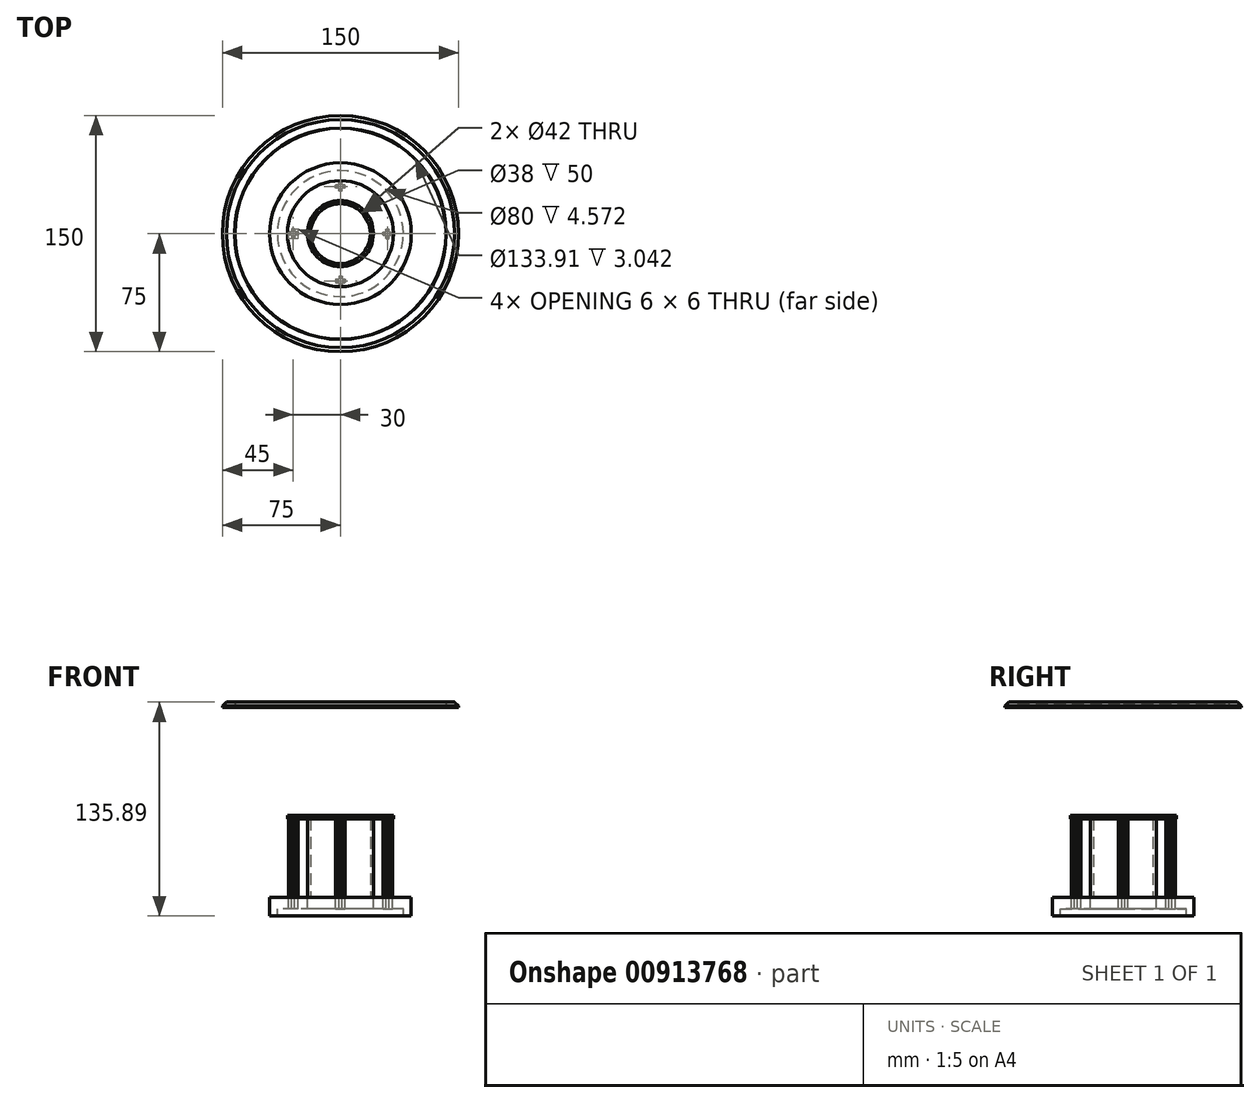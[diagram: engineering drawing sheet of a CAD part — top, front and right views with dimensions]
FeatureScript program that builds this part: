
annotation { "Feature Type Name" : "Feature", "Feature Type Description" : "" }
export const myFeature = defineFeature(function(context is Context, id is Id, definition is map)
    precondition{}
    {
        {
            var Q0;
            Q0=qCreatedBy(makeId("Top.planeOp"),FACE);
            var sketch = newSketch(context, id + "F0", { "sketchPlane" : qUnion([Q0])});
            skLineSegment(sketch, "E0.bottom", {"start": v(3, 29) * mm, "end": v(-3, 29) * mm});
            skLineSegment(sketch, "E0.top", {"start": v(3, 31) * mm, "end": v(-3, 31) * mm});
            skLineSegment(sketch, "E0.left", {"start": v(3, 29) * mm, "end": v(3, 31) * mm});
            skLineSegment(sketch, "E0.right", {"start": v(-3, 29) * mm, "end": v(-3, 31) * mm});
            skPoint(sketch, "E0.middle", {"position": v(0, 30) * mm});
            skLineSegment(sketch, "E1.bottom", {"start": v(1, 27) * mm, "end": v(-1, 27) * mm});
            skLineSegment(sketch, "E1.top", {"start": v(1, 33) * mm, "end": v(-1, 33) * mm});
            skLineSegment(sketch, "E1.left", {"start": v(1, 27) * mm, "end": v(1, 33) * mm});
            skLineSegment(sketch, "E1.right", {"start": v(-1, 27) * mm, "end": v(-1, 33) * mm});
            skLineSegment(sketch, "E2.1.0", {"start": v(-27, 1) * mm, "end": v(-27, -1) * mm});
            skLineSegment(sketch, "E2.1.1", {"start": v(-27, -1) * mm, "end": v(-33, -1) * mm});
            skLineSegment(sketch, "E2.1.2", {"start": v(-29, 3) * mm, "end": v(-29, -3) * mm});
            skLineSegment(sketch, "E2.1.3", {"start": v(-33, 1) * mm, "end": v(-33, -1) * mm});
            skLineSegment(sketch, "E2.1.4", {"start": v(-29, -3) * mm, "end": v(-31, -3) * mm});
            skLineSegment(sketch, "E2.1.5", {"start": v(-29, 3) * mm, "end": v(-31, 3) * mm});
            skLineSegment(sketch, "E2.1.6", {"start": v(-27, 1) * mm, "end": v(-33, 1) * mm});
            skLineSegment(sketch, "E2.1.7", {"start": v(-31, 3) * mm, "end": v(-31, -3) * mm});
            skPoint(sketch, "E2.1.8", {"position": v(-30, 0) * mm});
            skPoint(sketch, "E2.1.9", {"position": v(-30, 0) * mm});
            skLineSegment(sketch, "E2.2.0", {"start": v(-1, -27) * mm, "end": v(1, -27) * mm});
            skLineSegment(sketch, "E2.2.1", {"start": v(1, -27) * mm, "end": v(1, -33) * mm});
            skLineSegment(sketch, "E2.2.2", {"start": v(-3, -29) * mm, "end": v(3, -29) * mm});
            skLineSegment(sketch, "E2.2.3", {"start": v(-1, -33) * mm, "end": v(1, -33) * mm});
            skLineSegment(sketch, "E2.2.4", {"start": v(3, -29) * mm, "end": v(3, -31) * mm});
            skLineSegment(sketch, "E2.2.5", {"start": v(-3, -29) * mm, "end": v(-3, -31) * mm});
            skLineSegment(sketch, "E2.2.6", {"start": v(-1, -27) * mm, "end": v(-1, -33) * mm});
            skLineSegment(sketch, "E2.2.7", {"start": v(-3, -31) * mm, "end": v(3, -31) * mm});
            skPoint(sketch, "E2.2.8", {"position": v(0, -30) * mm});
            skPoint(sketch, "E2.2.9", {"position": v(0, -30) * mm});
            skLineSegment(sketch, "E2.3.0", {"start": v(27, -1) * mm, "end": v(27, 1) * mm});
            skLineSegment(sketch, "E2.3.1", {"start": v(27, 1) * mm, "end": v(33, 1) * mm});
            skLineSegment(sketch, "E2.3.2", {"start": v(29, -3) * mm, "end": v(29, 3) * mm});
            skLineSegment(sketch, "E2.3.3", {"start": v(33, -1) * mm, "end": v(33, 1) * mm});
            skLineSegment(sketch, "E2.3.4", {"start": v(29, 3) * mm, "end": v(31, 3) * mm});
            skLineSegment(sketch, "E2.3.5", {"start": v(29, -3) * mm, "end": v(31, -3) * mm});
            skLineSegment(sketch, "E2.3.6", {"start": v(27, -1) * mm, "end": v(33, -1) * mm});
            skLineSegment(sketch, "E2.3.7", {"start": v(31, -3) * mm, "end": v(31, 3) * mm});
            skPoint(sketch, "E2.3.8", {"position": v(30, 0) * mm});
            skPoint(sketch, "E2.3.9", {"position": v(30, 0) * mm});
            skPoint(sketch, "E2.center", {"position": v(0, 0) * mm});
            skCircle(sketch, "E3", {"center": v(0, 0) * mm, "radius": 21 * mm});
            skCircle(sketch, "E4", {"center": v(0, 0) * mm, "radius": 19 * mm});
            skCircle(sketch, "E5", {"center": v(0, 0) * mm, "radius": 45 * mm});
            skCircle(sketch, "E6", {"center": v(0, 0) * mm, "radius": 40 * mm});
            skCircle(sketch, "E7", {"center": v(0, 0) * mm, "radius": 10.99 * mm});
            skSolve(sketch);
        }
        {
            var Q0;
            {var subQ0=sQuery(id+"F0.wireOp",EDGE,"E0.right");Q0=makeQuery(id+"F0.imprint","IMPRINT",FACE,{"disambiguationData":[TD([[makeQuery(id+"F0.imprint","IMPRINT",EDGE,{"derivedFrom":subQ0}),-1.0]])]});}
            var Q1;
            {var subQ5=sQuery(id+"F0.wireOp",EDGE,"E1.top");Q1=makeQuery(id+"F0.imprint","IMPRINT",FACE,{"disambiguationData":[TD([[makeQuery(id+"F0.imprint","IMPRINT",EDGE,{"derivedFrom":subQ5}),1.0]])]});}
            var Q2;
            {var subQ0=sQuery(id+"F0.wireOp",EDGE,"E0.left");Q2=makeQuery(id+"F0.imprint","IMPRINT",FACE,{"disambiguationData":[TD([[makeQuery(id+"F0.imprint","IMPRINT",EDGE,{"derivedFrom":subQ0}),1.0]])]});}
            var Q3;
            {var subQ5=sQuery(id+"F0.wireOp",EDGE,"E1.bottom");Q3=makeQuery(id+"F0.imprint","IMPRINT",FACE,{"disambiguationData":[TD([[makeQuery(id+"F0.imprint","IMPRINT",EDGE,{"derivedFrom":subQ5}),-1.0]])]});}
            var Q4;
            {var subQ0=sQuery(id+"F0.wireOp",EDGE,"E1.left");var subQ1=sQuery(id+"F0.wireOp",EDGE,"E0.bottom");var subQ2=makeQuery(id+"F0.imprint","INTERSECT",VERTEX,{"derivedFrom":[subQ1,subQ0]});Q4=makeQuery(id+"F0.imprint","IMPRINT",FACE,{"disambiguationData":[TD([[makeQuery(id+"F0.imprint","IMPRINT",EDGE,{"disambiguationData":[TD([[subQ2,-1.0]])],"derivedFrom":subQ1}),-1.0]])]});}
            var Q5;
            {var subQ0=sQuery(id+"F0.wireOp",EDGE,"E2.3.3");Q5=makeQuery(id+"F0.imprint","IMPRINT",FACE,{"disambiguationData":[TD([[makeQuery(id+"F0.imprint","IMPRINT",EDGE,{"derivedFrom":subQ0}),1.0]])]});}
            var Q6;
            {var subQ0=sQuery(id+"F0.wireOp",EDGE,"E2.3.0");Q6=makeQuery(id+"F0.imprint","IMPRINT",FACE,{"disambiguationData":[TD([[makeQuery(id+"F0.imprint","IMPRINT",EDGE,{"derivedFrom":subQ0}),-1.0]])]});}
            var Q7;
            {var subQ0=sQuery(id+"F0.wireOp",EDGE,"E2.3.5");Q7=makeQuery(id+"F0.imprint","IMPRINT",FACE,{"disambiguationData":[TD([[makeQuery(id+"F0.imprint","IMPRINT",EDGE,{"derivedFrom":subQ0}),1.0]])]});}
            var Q8;
            {var subQ5=sQuery(id+"F0.wireOp",EDGE,"E2.3.4");Q8=makeQuery(id+"F0.imprint","IMPRINT",FACE,{"disambiguationData":[TD([[makeQuery(id+"F0.imprint","IMPRINT",EDGE,{"derivedFrom":subQ5}),-1.0]])]});}
            var Q9;
            {var subQ0=sQuery(id+"F0.wireOp",EDGE,"E2.3.2");var subQ1=sQuery(id+"F0.wireOp",EDGE,"E2.3.1");var subQ2=makeQuery(id+"F0.imprint","INTERSECT",VERTEX,{"derivedFrom":[subQ1,subQ0]});Q9=makeQuery(id+"F0.imprint","IMPRINT",FACE,{"disambiguationData":[TD([[makeQuery(id+"F0.imprint","IMPRINT",EDGE,{"disambiguationData":[TD([[subQ2,-1.0]])],"derivedFrom":subQ1}),-1.0]])]});}
            var Q10;
            {var subQ0=sQuery(id+"F0.wireOp",EDGE,"E2.2.0");Q10=makeQuery(id+"F0.imprint","IMPRINT",FACE,{"disambiguationData":[TD([[makeQuery(id+"F0.imprint","IMPRINT",EDGE,{"derivedFrom":subQ0}),-1.0]])]});}
            var Q11;
            {var subQ5=sQuery(id+"F0.wireOp",EDGE,"E2.2.4");Q11=makeQuery(id+"F0.imprint","IMPRINT",FACE,{"disambiguationData":[TD([[makeQuery(id+"F0.imprint","IMPRINT",EDGE,{"derivedFrom":subQ5}),-1.0]])]});}
            var Q12;
            {var subQ0=sQuery(id+"F0.wireOp",EDGE,"E2.2.5");Q12=makeQuery(id+"F0.imprint","IMPRINT",FACE,{"disambiguationData":[TD([[makeQuery(id+"F0.imprint","IMPRINT",EDGE,{"derivedFrom":subQ0}),1.0]])]});}
            var Q13;
            {var subQ0=sQuery(id+"F0.wireOp",EDGE,"E2.2.3");Q13=makeQuery(id+"F0.imprint","IMPRINT",FACE,{"disambiguationData":[TD([[makeQuery(id+"F0.imprint","IMPRINT",EDGE,{"derivedFrom":subQ0}),1.0]])]});}
            var Q14;
            {var subQ0=sQuery(id+"F0.wireOp",EDGE,"E2.2.2");var subQ1=sQuery(id+"F0.wireOp",EDGE,"E2.2.1");var subQ2=makeQuery(id+"F0.imprint","INTERSECT",VERTEX,{"derivedFrom":[subQ1,subQ0]});Q14=makeQuery(id+"F0.imprint","IMPRINT",FACE,{"disambiguationData":[TD([[makeQuery(id+"F0.imprint","IMPRINT",EDGE,{"disambiguationData":[TD([[subQ2,-1.0]])],"derivedFrom":subQ1}),-1.0]])]});}
            var Q15;
            {var subQ0=sQuery(id+"F0.wireOp",EDGE,"E2.1.5");Q15=makeQuery(id+"F0.imprint","IMPRINT",FACE,{"disambiguationData":[TD([[makeQuery(id+"F0.imprint","IMPRINT",EDGE,{"derivedFrom":subQ0}),1.0]])]});}
            var Q16;
            {var subQ0=sQuery(id+"F0.wireOp",EDGE,"E2.1.3");Q16=makeQuery(id+"F0.imprint","IMPRINT",FACE,{"disambiguationData":[TD([[makeQuery(id+"F0.imprint","IMPRINT",EDGE,{"derivedFrom":subQ0}),1.0]])]});}
            var Q17;
            {var subQ0=sQuery(id+"F0.wireOp",EDGE,"E2.1.0");Q17=makeQuery(id+"F0.imprint","IMPRINT",FACE,{"disambiguationData":[TD([[makeQuery(id+"F0.imprint","IMPRINT",EDGE,{"derivedFrom":subQ0}),-1.0]])]});}
            var Q18;
            {var subQ5=sQuery(id+"F0.wireOp",EDGE,"E2.1.4");Q18=makeQuery(id+"F0.imprint","IMPRINT",FACE,{"disambiguationData":[TD([[makeQuery(id+"F0.imprint","IMPRINT",EDGE,{"derivedFrom":subQ5}),-1.0]])]});}
            var Q19;
            {var subQ0=sQuery(id+"F0.wireOp",EDGE,"E2.1.2");var subQ1=sQuery(id+"F0.wireOp",EDGE,"E2.1.1");var subQ2=makeQuery(id+"F0.imprint","INTERSECT",VERTEX,{"derivedFrom":[subQ1,subQ0]});Q19=makeQuery(id+"F0.imprint","IMPRINT",FACE,{"disambiguationData":[TD([[makeQuery(id+"F0.imprint","IMPRINT",EDGE,{"disambiguationData":[TD([[subQ2,-1.0]])],"derivedFrom":subQ1}),-1.0]])]});}
            extrude(context, id + "F1", {"entities" : qUnion([Q0, Q1, Q2, Q3, Q4, Q5, Q6, Q7, Q8, Q9, Q10, Q11, Q12, Q13, Q14, Q15, Q16, Q17, Q18, Q19]), "depth" : 50 * mm, "offsetDistance" : 25.4 * mm});
        }
        {
            var Q0;
            Q0=makeQuery(id+"F0.imprint","IMPRINT",FACE,{"disambiguationData":[TD([[makeQuery(id+"F0.imprint","IMPRINT",EDGE,{"derivedFrom":sQuery(id+"F0.wireOp",EDGE,"E3")}),1.0]])]});
            extrude(context, id + "F2", {"entities" : qUnion([Q0]), "depth" : 50 * mm, "offsetDistance" : 25.4 * mm});
        }
        {
            var Q0;
            Q0=makeQuery(id+"F2.opExtrude","CAP_FACE",FACE,{"disambiguationData":[OSD([sQuery(id+"F0.wireOp",EDGE,"E3"),sQuery(id+"F0.wireOp",EDGE,"E4")])],"isStart":false});
            var sketch = newSketch(context, id + "F3", { "sketchPlane" : qUnion([Q0])});
            skCircle(sketch, "E8", {"center": v(0, 0) * mm, "radius": 33.67 * mm});
            skCircle(sketch, "E9", {"center": v(0, 0) * mm, "radius": 18.95 * mm});
            skSolve(sketch);
        }
        {
            var Q0;
            Q0=makeQuery(id+"F3.imprint","IMPRINT",FACE,{"disambiguationData":[TD([[makeQuery(id+"F3.imprint","IMPRINT",EDGE,{"derivedFrom":sQuery(id+"F3.wireOp",EDGE,"E8")}),1.0]])]});
            extrude(context, id + "F4", {"entities" : qUnion([Q0]), "depth" : 2.3 * mm, "offsetDistance" : 25.4 * mm});
        }
        {
            var Q0;
            Q0=makeQuery(id+"F0.imprint","IMPRINT",FACE,{"disambiguationData":[TD([[makeQuery(id+"F0.imprint","IMPRINT",EDGE,{"derivedFrom":sQuery(id+"F0.wireOp",EDGE,"E7")}),1.0]])]});
            var Q1;
            Q1=sQuery(id+"F0.wireOp",EDGE,"E7");
            extrude(context, id + "F5", {"entities" : qUnion([Q0]), "surfaceEntities" : qUnion([Q1]), "depth" : 120.65 * mm, "offsetDistance" : 25.4 * mm});
        }
        {
            var Q0;
            Q0=makeQuery(id+"F5.opExtrude","CAP_FACE",FACE,{"disambiguationData":[OSD([sQuery(id+"F0.wireOp",EDGE,"E7")])],"isStart":false});
            var sketch = newSketch(context, id + "F6", { "sketchPlane" : qUnion([Q0])});
            skCircle(sketch, "E10", {"center": v(0, 0) * mm, "radius": 66.96 * mm});
            skCircle(sketch, "E11", {"center": v(0, 0) * mm, "radius": 75 * mm});
            skSolve(sketch);
        }
        {
            var Q0;
            Q0 = qSketchRegion(id + "F6", true);
            extrude(context, id + "F7", {"entities" : qUnion([Q0]), "depth" : 3.56 * mm, "offsetDistance" : 25.4 * mm});
        }
        {
            var Q0;
            Q0=makeQuery(id+"F5.opExtrude","SWEPT_BODY",BODY,{"disambiguationData":[OSD([sQuery(id+"F0.wireOp",EDGE,"E7")])]});
            deleteBodies(context, id + "F8", {"entities" : qUnion([Q0])});
        }
        {
            var Q0;
            Q0=qCreatedBy(makeId("Front.planeOp"),FACE);
            var sketch = newSketch(context, id + "F9", { "sketchPlane" : qUnion([Q0])});
            skLineSegment(sketch, "E12", {"start": v(-74.9, 120.65) * mm, "end": v(-33.67, 52.29) * mm});
            skLineSegment(sketch, "E13", {"start": v(0, 54.54) * mm, "end": v(0, 130.04) * mm, "construction": true});
            skLineSegment(sketch, "E14", {"start": v(-73.63, 120.69) * mm, "end": v(-32.42, 52.37) * mm});
            skLineSegment(sketch, "E15", {"start": v(-32.42, 52.37) * mm, "end": v(-33.67, 52.29) * mm});
            skSolve(sketch);
        }
        {
            var Q0;
            Q0=sQuery(id+"F9.wireOp",EDGE,"E12");
            var Q1;
            Q1=sQuery(id+"F9.wireOp",EDGE,"E13");
            revolve(context, id + "F10", {"bodyType" : ToolBodyType.SURFACE, "surfaceOperationType" : NewSurfaceOperationType.NEW, "surfaceEntities" : qUnion([Q0]), "axis" : qUnion([Q1]), "revolveType" : RevolveType.FULL});
        }
        {
            var Q0;
            Q0=makeQuery(id+"F0.imprint","IMPRINT",FACE,{"disambiguationData":[TD([[makeQuery(id+"F0.imprint","IMPRINT",EDGE,{"derivedFrom":sQuery(id+"F0.wireOp",EDGE,"E5")}),1.0]])]});
            extrude(context, id + "F11", {"entities" : qUnion([Q0]), "oppositeDirection" : true, "depth" : 11.68 * mm, "offsetDistance" : 25.4 * mm});
        }
        {
            var Q0;
            {var subQ38=sQuery(id+"F0.wireOp",EDGE,"E0.left");Q0=makeQuery(id+"F0.imprint","IMPRINT",FACE,{"disambiguationData":[TD([[makeQuery(id+"F0.imprint","IMPRINT",EDGE,{"derivedFrom":subQ38}),-1.0]])]});}
            extrude(context, id + "F12", {"entities" : qUnion([Q0]), "operationType" : NewBodyOperationType.ADD, "oppositeDirection" : true, "depth" : 7.11 * mm, "offsetDistance" : 25.4 * mm});
        }
        {
            var Q0;
            Q0=makeQuery(id+"F7.opExtrude","CAP_EDGE",EDGE,{"disambiguationData":[OSD([sQuery(id+"F6.wireOp",EDGE,"E11")])],"isStart":false});
            chamfer(context, id + "F13", {"entities" : qUnion([Q0]), "width" : 2.54 * mm, "tangentPropagation" : true});
        }
        {
            var Q0;
            Q0=makeQuery(id+"F7.opExtrude","CAP_EDGE",EDGE,{"disambiguationData":[OSD([sQuery(id+"F6.wireOp",EDGE,"E10")])],"isStart":false});
            chamfer(context, id + "F14", {"entities" : qUnion([Q0]), "width" : .1 * mm, "tangentPropagation" : true});
        }
        {
            var Q0;
            {var subQ0=sQuery(id+"F6.wireOp",EDGE,"E10");Q0=makeQuery(id+"F14.opChamfer","BLEND_EDGE",EDGE,{"blendedFrom":[makeQuery(id+"F7.opExtrude","CAP_EDGE",EDGE,{"disambiguationData":[OSD([subQ0])],"isStart":false}),makeQuery(id+"F7.opExtrude","SWEPT_FACE",FACE,{"disambiguationData":[OSD([subQ0])]})],"blendedInto":[makeQuery(id+"F7.opExtrude","SWEPT_FACE",FACE,{"disambiguationData":[OSD([subQ0])]})]});}
            chamfer(context, id + "F15", {"entities" : qUnion([Q0]), "width" : 1 * mm, "tangentPropagation" : true});
        }
    });
